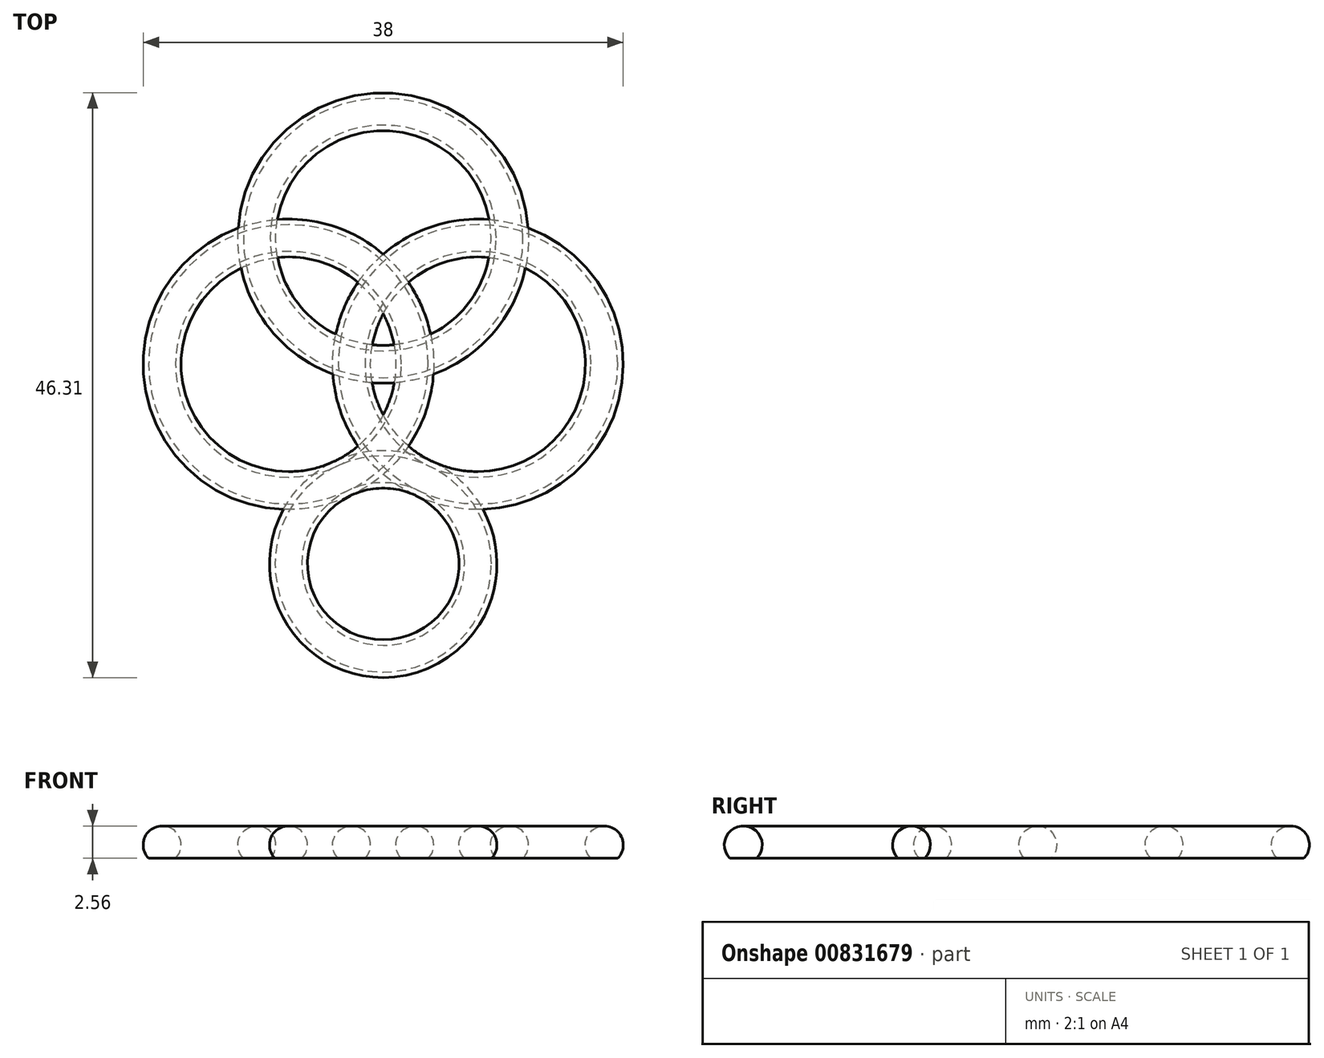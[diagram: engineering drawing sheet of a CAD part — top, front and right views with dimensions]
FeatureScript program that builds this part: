
annotation { "Feature Type Name" : "Feature", "Feature Type Description" : "" }
export const myFeature = defineFeature(function(context is Context, id is Id, definition is map)
    precondition{}
    {
        {
            var Q0;
            Q0=qCreatedBy(makeId("Top.planeOp"),FACE);
            var sketch = newSketch(context, id + "F0", { "sketchPlane" : qUnion([Q0])});
            skCircle(sketch, "E0", {"center": v(0, 0) * mm, "radius": 7.5 * mm});
            skCircle(sketch, "E1", {"center": v(-7.5, 15.81) * mm, "radius": 10 * mm});
            skCircle(sketch, "E2.MirrorC", {"center": v(7.5, 15.81) * mm, "radius": 10 * mm});
            skCircle(sketch, "E3", {"center": v(0, 25.81) * mm, "radius": 10 * mm});
            skLineSegment(sketch, "E4", {"start": v(-7.5, 15.81) * mm, "end": v(7.5, 15.81) * mm, "construction": true});
            skSolve(sketch);
        }
        {
            var Q0;
            Q0=qCreatedBy(makeId("Right.planeOp"),FACE);
            var sketch = newSketch(context, id + "F1", { "sketchPlane" : qUnion([Q0])});
            skLineSegment(sketch, "E5.0", {"start": v(-7.5, 0) * mm, "end": v(12.5, 0) * mm});
            skArc(sketch, "E6", {"start": v(-6.44, -1.06) * mm, "mid": v(-7.5, 1.5) * mm, "end": v(-8.56, -1.06) * mm});
            skLineSegment(sketch, "E7", {"start": v(-8.56, -1.06) * mm, "end": v(-6.44, -1.06) * mm});
            skLineSegment(sketch, "E8", {"start": v(-6.44, -1.06) * mm, "end": v(-3.6, 1.79) * mm, "construction": true});
            skSolve(sketch);
        }
        {
            var Q0;
            {var subQ0=sQuery(id+"F1.wireOp",EDGE,"E7");Q0=makeQuery(id+"F1.imprint","IMPRINT",FACE,{"disambiguationData":[TD([[makeQuery(id+"F1.imprint","IMPRINT",EDGE,{"derivedFrom":subQ0}),1.0]])]});}
            var Q1;
            Q1=sQuery(id+"F0.wireOp",EDGE,"E0");
            sweep(context, id + "F2", {"profiles" : qUnion([Q0]), "path" : qUnion([Q1])});
        }
        {
            var Q0;
            Q0=qCreatedBy(makeId("Right.planeOp"),FACE);
            var sketch = newSketch(context, id + "F3", { "sketchPlane" : qUnion([Q0])});
            skLineSegment(sketch, "E9.0", {"start": v(15.81, 0) * mm, "end": v(35.81, 0) * mm});
            skArc(sketch, "E10", {"start": v(16.87, -1.06) * mm, "mid": v(15.81, 1.5) * mm, "end": v(14.75, -1.06) * mm});
            skLineSegment(sketch, "E11", {"start": v(14.75, -1.06) * mm, "end": v(16.87, -1.06) * mm});
            skLineSegment(sketch, "E12", {"start": v(16.87, -1.06) * mm, "end": v(19.72, 1.79) * mm, "construction": true});
            skSolve(sketch);
        }
        {
            var Q0;
            {var subQ0=sQuery(id+"F3.wireOp",EDGE,"E11");Q0=makeQuery(id+"F3.imprint","IMPRINT",FACE,{"disambiguationData":[TD([[makeQuery(id+"F3.imprint","IMPRINT",EDGE,{"derivedFrom":subQ0}),1.0]])]});}
            var Q1;
            Q1=sQuery(id+"F0.wireOp",EDGE,"E3");
            sweep(context, id + "F4", {"profiles" : qUnion([Q0]), "path" : qUnion([Q1])});
        }
        {
            var Q0;
            Q0=makeQuery(id+"F4.opSweep","SWEPT_BODY",BODY,{"disambiguationData":[OSD([sQuery(id+"F0.wireOp",EDGE,"E3"),sQuery(id+"F3.wireOp",EDGE,"E10"),sQuery(id+"F3.wireOp",EDGE,"E11")])]});
            var Q1;
            Q1=sQuery(id+"F0.wireOp",VERTEX,"E3.center");
            var Q2;
            Q2=sQuery(id+"F0.wireOp",VERTEX,"E4.start");
            transform(context, id + "F5", {"entities" : qUnion([Q0]), "transformType" : TransformType.TRANSLATION_ENTITY, "oppositeDirectionEntity" : false, "transformLine" : qUnion([Q1, Q2]), "makeCopy" : true});
        }
        {
            var Q0;
            Q0=makeQuery(id+"F4.opSweep","SWEPT_BODY",BODY,{"disambiguationData":[OSD([sQuery(id+"F0.wireOp",EDGE,"E3"),sQuery(id+"F3.wireOp",EDGE,"E10"),sQuery(id+"F3.wireOp",EDGE,"E11")])]});
            var Q1;
            Q1=sQuery(id+"F0.wireOp",VERTEX,"E3.center");
            var Q2;
            Q2=sQuery(id+"F0.wireOp",VERTEX,"E4.end");
            transform(context, id + "F6", {"entities" : qUnion([Q0]), "transformType" : TransformType.TRANSLATION_ENTITY, "oppositeDirectionEntity" : false, "transformLine" : qUnion([Q1, Q2]), "makeCopy" : true});
        }
    });
